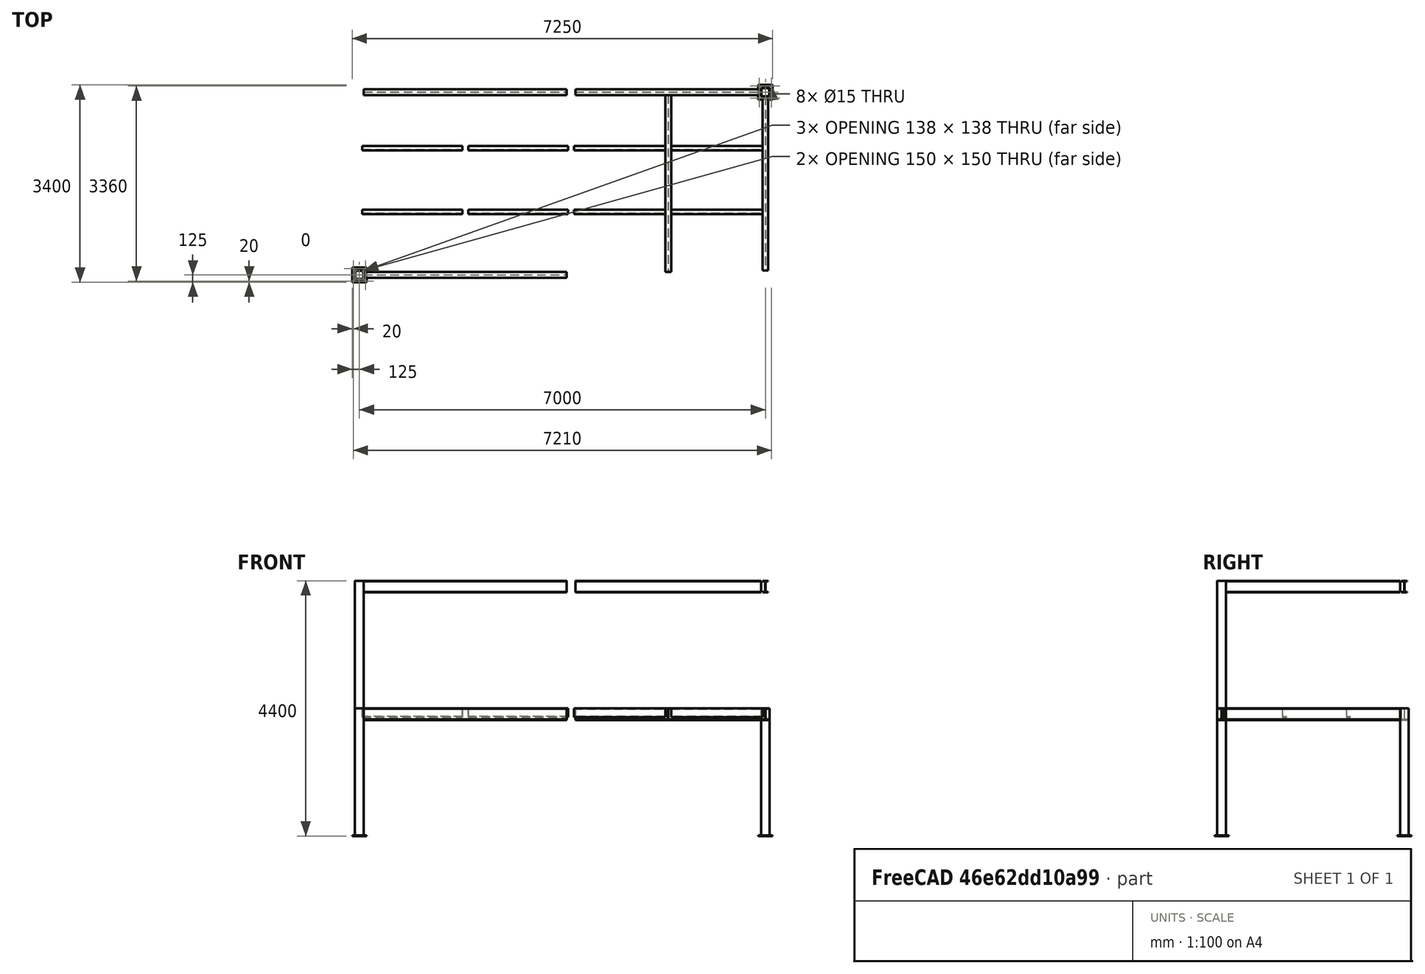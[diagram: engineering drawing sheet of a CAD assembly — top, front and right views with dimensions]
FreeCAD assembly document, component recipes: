
FREECAD ASSEMBLY — COMPONENT RECIPES ("steelframe2")

This assembly document has 8 components, labeled P0..P7 below (a component is one placed body or linked part). 0 of them carry a construction recipe — the FreeCAD feature program that regenerates the part from scratch, quoted from this document or its linked companion documents; the rest are supplied as boundary geometry only. No exploded tour is included for this assembly.
COMPONENT P0 — geometry summary ("Square-steel pipe002"; no construction recipe available for this part):
  bounding box: 2200.0 x 250.0 x 250.0 mm
  tessellated surface: 596 triangles
  volume: 7925111 mm^3 (6% of its bounding box)
  symmetry: 4-fold rotationally symmetric about the z axis; mirror-symmetric across its x mid-plane, y mid-plane
COMPONENT P1 — geometry summary ("Square-steel pipe003"; no construction recipe available for this part):
  bounding box: 2200.0 x 250.0 x 250.0 mm
  tessellated surface: 596 triangles
  volume: 7925111 mm^3 (6% of its bounding box)
  symmetry: 4-fold rotationally symmetric about the z axis; mirror-symmetric across its x mid-plane, y mid-plane
COMPONENT P2 — geometry summary ("H_thin003"; no construction recipe available for this part):
  bounding box: 3500.0 x 200.0 x 100.0 mm
  tessellated surface: 140 triangles
  volume: 9505536 mm^3 (14% of its bounding box)
  symmetry: 2-fold rotationally symmetric about the x axis; 2-fold rotationally symmetric about the y axis; 2-fold rotationally symmetric about the z axis; mirror-symmetric across its x mid-plane, y mid-plane, z mid-plane
COMPONENT P3 — geometry summary ("Square-steel pipe004"; no construction recipe available for this part):
  bounding box: 2200.0 x 250.0 x 250.0 mm
  tessellated surface: 596 triangles
  volume: 7925111 mm^3 (6% of its bounding box)
  symmetry: 4-fold rotationally symmetric about the z axis; mirror-symmetric across its x mid-plane, y mid-plane
COMPONENT P4 — geometry summary ("SQ_Pipe001"; no construction recipe available for this part):
  bounding box: 2200.0 x 150.0 x 150.0 mm
  tessellated surface: 208 triangles
  volume: 7399242 mm^3 (15% of its bounding box)
  symmetry: 2-fold rotationally symmetric about the x axis; 2-fold rotationally symmetric about the y axis; 4-fold rotationally symmetric about the z axis; mirror-symmetric across its x mid-plane, y mid-plane, z mid-plane
COMPONENT P5 — geometry summary ("SQ_Pipe005"; no construction recipe available for this part):
  bounding box: 2200.0 x 150.0 x 150.0 mm
  tessellated surface: 208 triangles
  volume: 7399242 mm^3 (15% of its bounding box)
  symmetry: 2-fold rotationally symmetric about the x axis; 2-fold rotationally symmetric about the y axis; 4-fold rotationally symmetric about the z axis; mirror-symmetric across its x mid-plane, y mid-plane, z mid-plane
COMPONENT P6 — geometry summary ("H_thin009"; no construction recipe available for this part):
  bounding box: 3500.0 x 200.0 x 100.0 mm
  tessellated surface: 140 triangles
  volume: 9505536 mm^3 (14% of its bounding box)
  symmetry: 2-fold rotationally symmetric about the x axis; 2-fold rotationally symmetric about the y axis; 2-fold rotationally symmetric about the z axis; mirror-symmetric across its x mid-plane, y mid-plane, z mid-plane
COMPONENT P7 — geometry summary ("H_thin010"; no construction recipe available for this part):
  bounding box: 3000.0 x 200.0 x 100.0 mm
  tessellated surface: 140 triangles
  volume: 8147602 mm^3 (14% of its bounding box)
  symmetry: 2-fold rotationally symmetric about the x axis; 2-fold rotationally symmetric about the y axis; 2-fold rotationally symmetric about the z axis; mirror-symmetric across its x mid-plane, y mid-plane, z mid-plane
PROVENANCE & LICENSES
A FreeCAD (.FCStd) document from a public repository crawl; recipes are the document's own serialized feature recipes (and, for linked parts, companion documents' recipes).
License: as declared in the source repository (recorded in the dataset sidecar).
